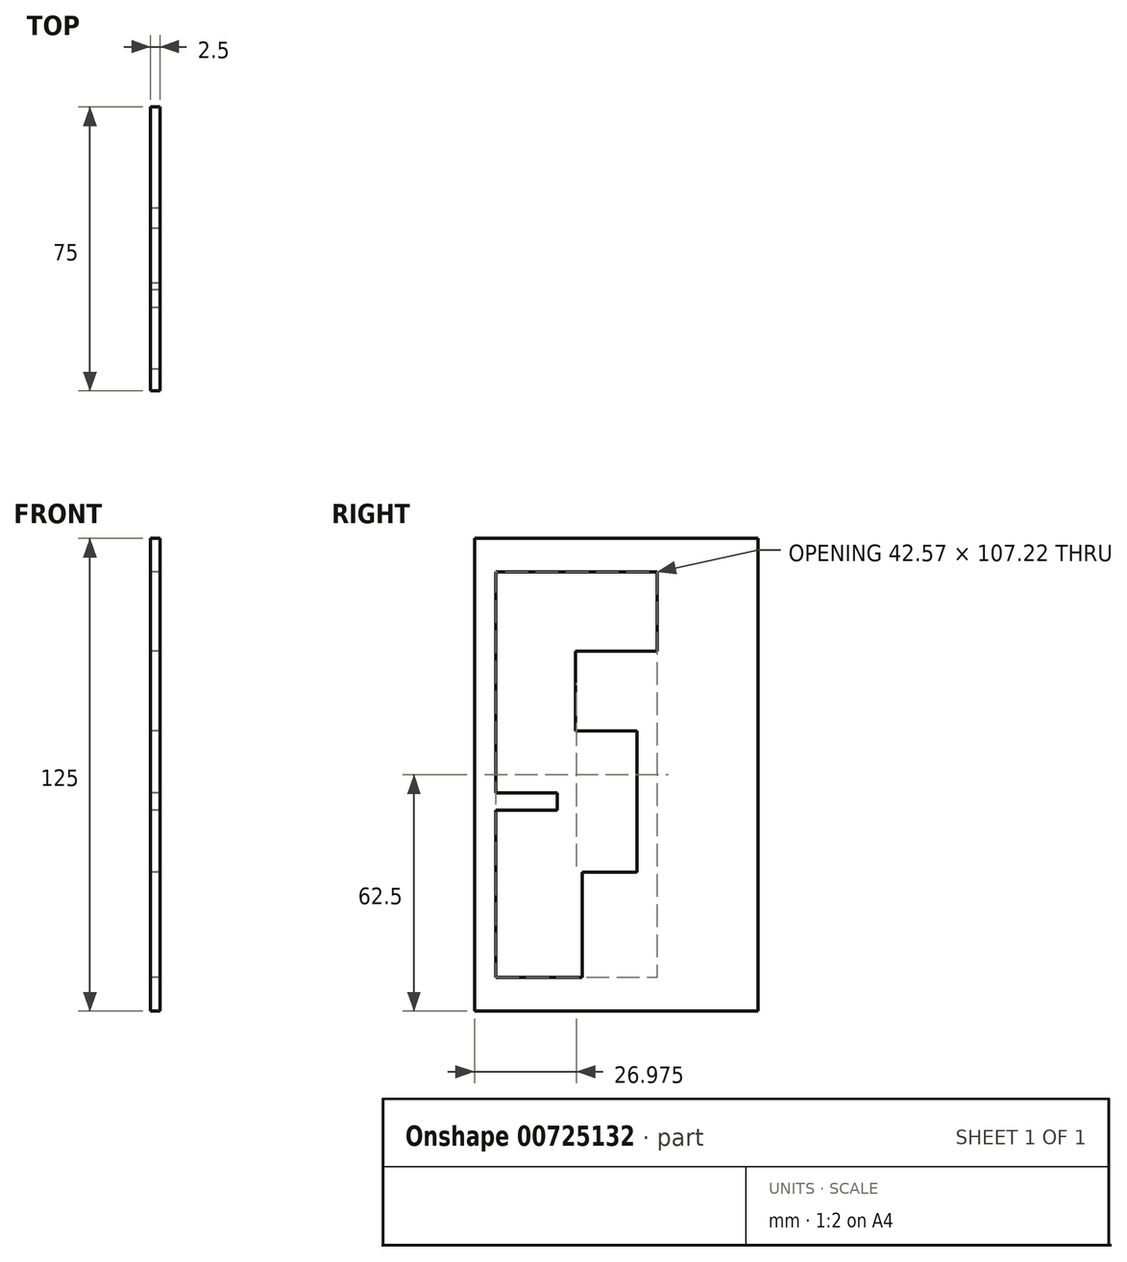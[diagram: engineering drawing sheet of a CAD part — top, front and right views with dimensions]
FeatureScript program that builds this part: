
annotation { "Feature Type Name" : "Feature", "Feature Type Description" : "" }
export const myFeature = defineFeature(function(context is Context, id is Id, definition is map)
    precondition{}
    {
        {
            var Q0;
            Q0=qCreatedBy(makeId("Right.planeOp"),FACE);
            var sketch = newSketch(context, id + "F0", { "sketchPlane" : qUnion([Q0])});
            skLineSegment(sketch, "E0.bottom", {"start": v(0, 0) * mm, "end": v(75, 0) * mm});
            skLineSegment(sketch, "E0.left", {"start": v(0, 0) * mm, "end": v(0, 125) * mm});
            skLineSegment(sketch, "E1.top", {"start": v(3.8, 3.81) * mm, "end": v(71.19, 3.81) * mm});
            skLineSegment(sketch, "E1.left", {"start": v(3.8, 121.19) * mm, "end": v(3.8, 3.8) * mm});
            skLineSegment(sketch, "E2.top", {"start": v(0, 125) * mm, "end": v(44.5, 125) * mm});
            skLineSegment(sketch, "E3", {"start": v(3.8, 121.19) * mm, "end": v(44.5, 121.19) * mm});
            skLineSegment(sketch, "E4", {"start": v(44.5, 125) * mm, "end": v(50.19, 125) * mm});
            skLineSegment(sketch, "E5", {"start": v(50.19, 121.19) * mm, "end": v(44.5, 121.19) * mm});
            skLineSegment(sketch, "E6", {"start": v(71.19, 3.81) * mm, "end": v(71.19, 125) * mm});
            skLineSegment(sketch, "E7", {"start": v(71.19, 125) * mm, "end": v(75, 125) * mm});
            skLineSegment(sketch, "E8", {"start": v(75, 125) * mm, "end": v(75, 0) * mm});
            skLineSegment(sketch, "E9", {"start": v(49.4, 121.19) * mm, "end": v(71.19, 121.19) * mm});
            skLineSegment(sketch, "E10", {"start": v(49.4, 125) * mm, "end": v(71.19, 125) * mm});
            skLineSegment(sketch, "E11", {"start": v(48.26, 116.11) * mm, "end": v(48.26, 95.11) * mm});
            skLineSegment(sketch, "E12", {"start": v(48.26, 116.11) * mm, "end": v(5.7, 116.11) * mm});
            skLineSegment(sketch, "E13", {"start": v(5.7, 116.1) * mm, "end": v(5.7, 53.1) * mm});
            skLineSegment(sketch, "E14", {"start": v(5.7, 53.1) * mm, "end": v(21.94, 53.1) * mm});
            skLineSegment(sketch, "E15", {"start": v(21.94, 57.77) * mm, "end": v(21.94, 53.1) * mm});
            skLineSegment(sketch, "E16", {"start": v(21.94, 57.77) * mm, "end": v(5.7, 57.77) * mm});
            skLineSegment(sketch, "E17", {"start": v(5.7, 57.77) * mm, "end": v(5.7, 8.89) * mm});
            skLineSegment(sketch, "E18", {"start": v(5.7, 8.89) * mm, "end": v(28.44, 8.89) * mm});
            skLineSegment(sketch, "E19", {"start": v(28.44, 8.89) * mm, "end": v(28.44, 36.77) * mm});
            skLineSegment(sketch, "E20", {"start": v(28.44, 36.77) * mm, "end": v(42.94, 36.77) * mm});
            skLineSegment(sketch, "E21", {"start": v(42.94, 36.77) * mm, "end": v(42.94, 74.11) * mm});
            skLineSegment(sketch, "E22", {"start": v(42.94, 74.11) * mm, "end": v(26.7, 74.1) * mm});
            skLineSegment(sketch, "E23", {"start": v(26.7, 74.1) * mm, "end": v(26.7, 95.11) * mm});
            skLineSegment(sketch, "E24", {"start": v(26.7, 95.11) * mm, "end": v(48.26, 95.11) * mm});
            skSolve(sketch);
        }
        {
            var Q0;
            Q0 = qSketchRegion(id + "F0", true);
            var Q1;
            {var subQ2=sQuery(id+"F0.wireOp",EDGE,"E1.top");Q1=makeQuery(id+"F0.imprint","IMPRINT",FACE,{"disambiguationData":[TD([[makeQuery(id+"F0.imprint","IMPRINT",EDGE,{"derivedFrom":subQ2}),1.0]])]});}
            var Q2;
            {var subQ0=sQuery(id+"F0.wireOp",EDGE,"E14");Q2=makeQuery(id+"F0.imprint","IMPRINT",FACE,{"disambiguationData":[TD([[makeQuery(id+"F0.imprint","IMPRINT",EDGE,{"derivedFrom":subQ0}),1.0]])]});}
            extrude(context, id + "F1", {"entities" : qUnion([Q0, Q1, Q2]), "depth" : 2.5 * mm, "offsetDistance" : 25.4 * mm});
        }
    });
